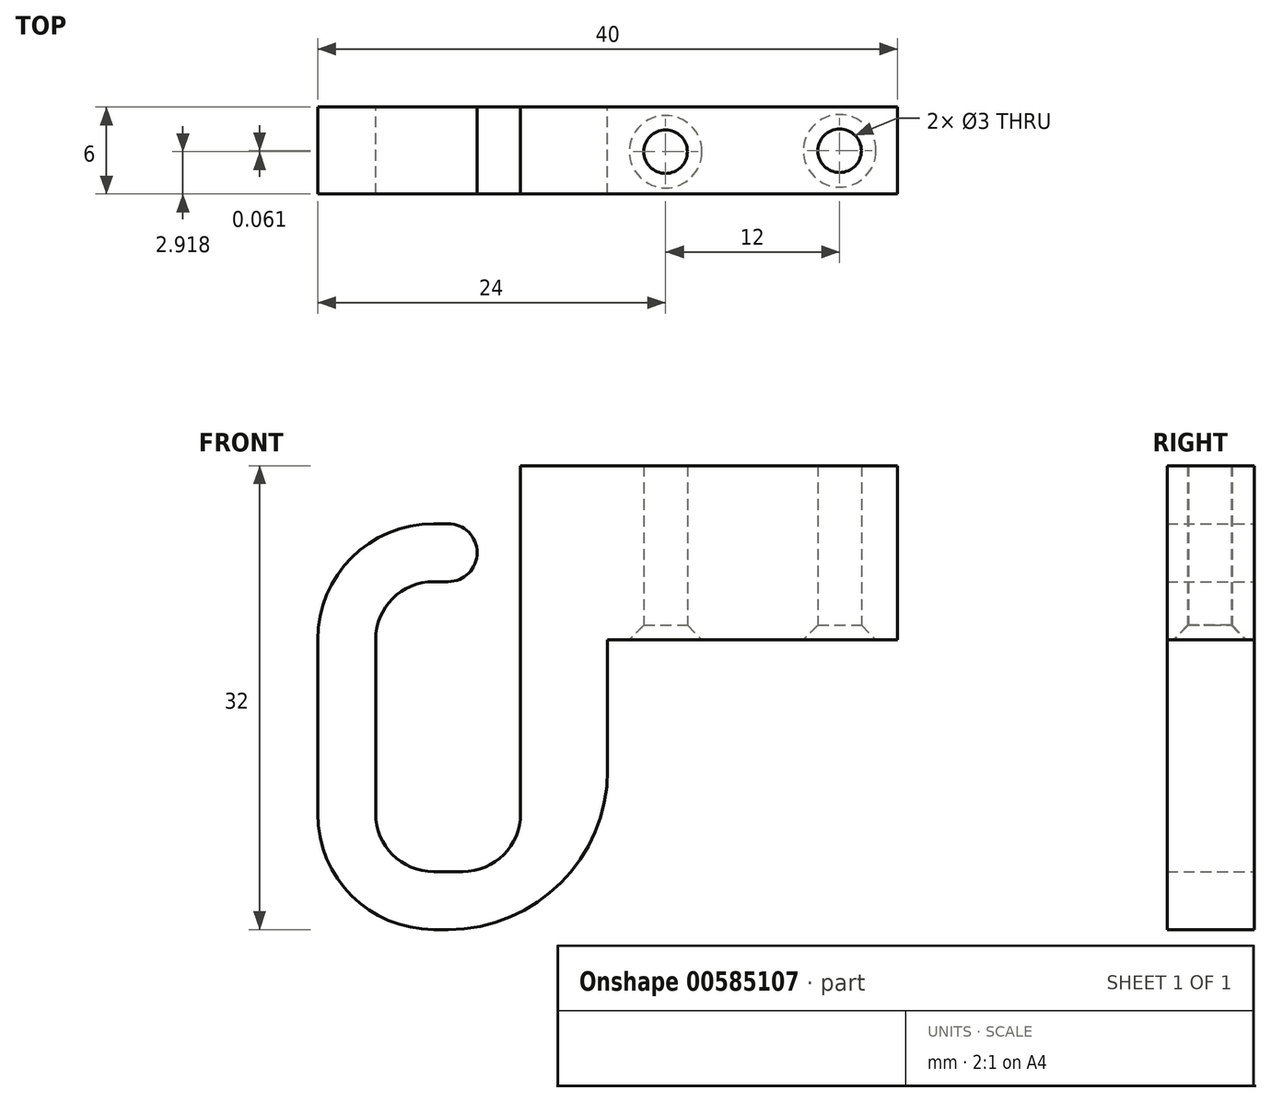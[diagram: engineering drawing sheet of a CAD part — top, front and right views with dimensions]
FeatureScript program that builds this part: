
annotation { "Feature Type Name" : "Feature", "Feature Type Description" : "" }
export const myFeature = defineFeature(function(context is Context, id is Id, definition is map)
    precondition{}
    {
        {
            var Q0;
            Q0=qCreatedBy(makeId("Front.planeOp"),FACE);
            var sketch = newSketch(context, id + "F0", { "sketchPlane" : qUnion([Q0])});
            skLineSegment(sketch, "E0", {"start": v(0, 20) * mm, "end": v(0, 0) * mm});
            skLineSegment(sketch, "E1", {"start": v(0, 0) * mm, "end": v(10, 0) * mm});
            skLineSegment(sketch, "E2", {"start": v(10, 0) * mm, "end": v(10, 28) * mm});
            skLineSegment(sketch, "E3", {"start": v(10, 28) * mm, "end": v(36, 28) * mm});
            skLineSegment(sketch, "E4", {"start": v(36, 28) * mm, "end": v(36, 16) * mm});
            skLineSegment(sketch, "E5", {"start": v(36, 16) * mm, "end": v(16, 16) * mm});
            skLineSegment(sketch, "E6", {"start": v(16, 16) * mm, "end": v(16, -4) * mm});
            skLineSegment(sketch, "E7", {"start": v(16, -4) * mm, "end": v(-4, -4) * mm});
            skLineSegment(sketch, "E8", {"start": v(-4, -4) * mm, "end": v(-4, 24) * mm});
            skLineSegment(sketch, "E9", {"start": v(-4, 24) * mm, "end": v(7, 24) * mm});
            skLineSegment(sketch, "E10", {"start": v(7, 24) * mm, "end": v(7, 20) * mm});
            skLineSegment(sketch, "E11", {"start": v(7, 20) * mm, "end": v(0, 20) * mm});
            skSolve(sketch);
        }
        {
            var Q0;
            Q0 = qSketchRegion(id + "F0", true);
            extrude(context, id + "F1", {"entities" : qUnion([Q0]), "depth" : 6 * mm, "offsetDistance" : 25 * mm});
        }
        {
            var Q0;
            Q0=makeQuery(id+"F1.opExtrude","SWEPT_EDGE",EDGE,{"disambiguationData":[OSD([sQuery(id+"F0.wireOp",EDGE,"E1"),sQuery(id+"F0.wireOp",EDGE,"E2")])]});
            var Q1;
            Q1=makeQuery(id+"F1.opExtrude","SWEPT_EDGE",EDGE,{"disambiguationData":[OSD([sQuery(id+"F0.wireOp",EDGE,"E0"),sQuery(id+"F0.wireOp",EDGE,"E1")])]});
            var Q2;
            Q2=makeQuery(id+"F1.opExtrude","SWEPT_EDGE",EDGE,{"disambiguationData":[OSD([sQuery(id+"F0.wireOp",EDGE,"E0"),sQuery(id+"F0.wireOp",EDGE,"E11")])]});
            fillet(context, id + "F2", {"entities" : qUnion([Q0, Q1, Q2]), "tangentPropagation" : true, "radius" : 4 * mm, "defaultsChanged" : true, "vertexSettings" : [], "allowEdgeOverflow" : false});
        }
        {
            var Q0;
            Q0=makeQuery(id+"F1.opExtrude","SWEPT_EDGE",EDGE,{"disambiguationData":[OSD([sQuery(id+"F0.wireOp",EDGE,"E8"),sQuery(id+"F0.wireOp",EDGE,"E9")])]});
            var Q1;
            Q1=makeQuery(id+"F1.opExtrude","SWEPT_EDGE",EDGE,{"disambiguationData":[OSD([sQuery(id+"F0.wireOp",EDGE,"E7"),sQuery(id+"F0.wireOp",EDGE,"E8")])]});
            fillet(context, id + "F3", {"entities" : qUnion([Q0, Q1]), "tangentPropagation" : true, "radius" : 8 * mm, "defaultsChanged" : true, "vertexSettings" : [], "allowEdgeOverflow" : false});
        }
        {
            var Q0;
            Q0=makeQuery(id+"F1.opExtrude","SWEPT_EDGE",EDGE,{"disambiguationData":[OSD([sQuery(id+"F0.wireOp",EDGE,"E6"),sQuery(id+"F0.wireOp",EDGE,"E7")])]});
            fillet(context, id + "F4", {"entities" : qUnion([Q0]), "tangentPropagation" : true, "radius" : 11 * mm, "defaultsChanged" : true, "vertexSettings" : [], "allowEdgeOverflow" : false});
        }
        {
            var Q0;
            Q0=makeQuery(id+"F1.opExtrude","SWEPT_EDGE",EDGE,{"disambiguationData":[OSD([sQuery(id+"F0.wireOp",EDGE,"E9"),sQuery(id+"F0.wireOp",EDGE,"E10")])]});
            var Q1;
            Q1=makeQuery(id+"F1.opExtrude","SWEPT_EDGE",EDGE,{"disambiguationData":[OSD([sQuery(id+"F0.wireOp",EDGE,"E10"),sQuery(id+"F0.wireOp",EDGE,"E11")])]});
            fillet(context, id + "F5", {"entities" : qUnion([Q0, Q1]), "tangentPropagation" : true, "radius" : 2 * mm, "defaultsChanged" : false, "vertexSettings" : [], "allowEdgeOverflow" : false});
        }
        {
            var Q0;
            Q0=makeQuery(id+"F1.opExtrude","SWEPT_FACE",FACE,{"disambiguationData":[OSD([sQuery(id+"F0.wireOp",EDGE,"E5")])]});
            var sketch = newSketch(context, id + "F6", { "sketchPlane" : qUnion([Q0])});
            skPoint(sketch, "E12", {"position": v(20, 3.08) * mm});
            skPoint(sketch, "E13", {"position": v(32, 3.02) * mm});
            skLineSegment(sketch, "E14", {"start": v(36, 3) * mm, "end": v(32, 3.02) * mm});
            skLineSegment(sketch, "E15", {"start": v(32, 3.02) * mm, "end": v(20, 3.08) * mm});
            skSolve(sketch);
        }
        {
            var Q0;
            Q0=sQuery(id+"F6.wireOp",VERTEX,"E15.end");
            var Q1;
            Q1=sQuery(id+"F6.wireOp",VERTEX,"E13");
            var Q2;
            Q2=makeQuery(id+"F1.opExtrude","SWEPT_BODY",BODY,{"disambiguationData":[OSD([sQuery(id+"F0.wireOp",EDGE,"E0"),sQuery(id+"F0.wireOp",EDGE,"E1"),sQuery(id+"F0.wireOp",EDGE,"E2"),sQuery(id+"F0.wireOp",EDGE,"E3"),sQuery(id+"F0.wireOp",EDGE,"E4"),sQuery(id+"F0.wireOp",EDGE,"E5"),sQuery(id+"F0.wireOp",EDGE,"E6"),sQuery(id+"F0.wireOp",EDGE,"E7"),sQuery(id+"F0.wireOp",EDGE,"E8"),sQuery(id+"F0.wireOp",EDGE,"E9"),sQuery(id+"F0.wireOp",EDGE,"E10"),sQuery(id+"F0.wireOp",EDGE,"E11")])]});
            hole(context, id + "F7", {"style" : HoleStyle.C_SINK, "endStyle" : HoleEndStyle.THROUGH, "holeDiameter" : 3 * mm, "cSinkDiameter" : 5 * mm, "cSinkAngle" : 90 * degree, "majorDiameter" : 5 * mm, "isTappedThrough" : true, "tappedDepth" : 12 * mm, "tapClearance" : 3, "locations" : qUnion([Q0, Q1]), "scope" : qUnion([Q2])});
        }
    });
